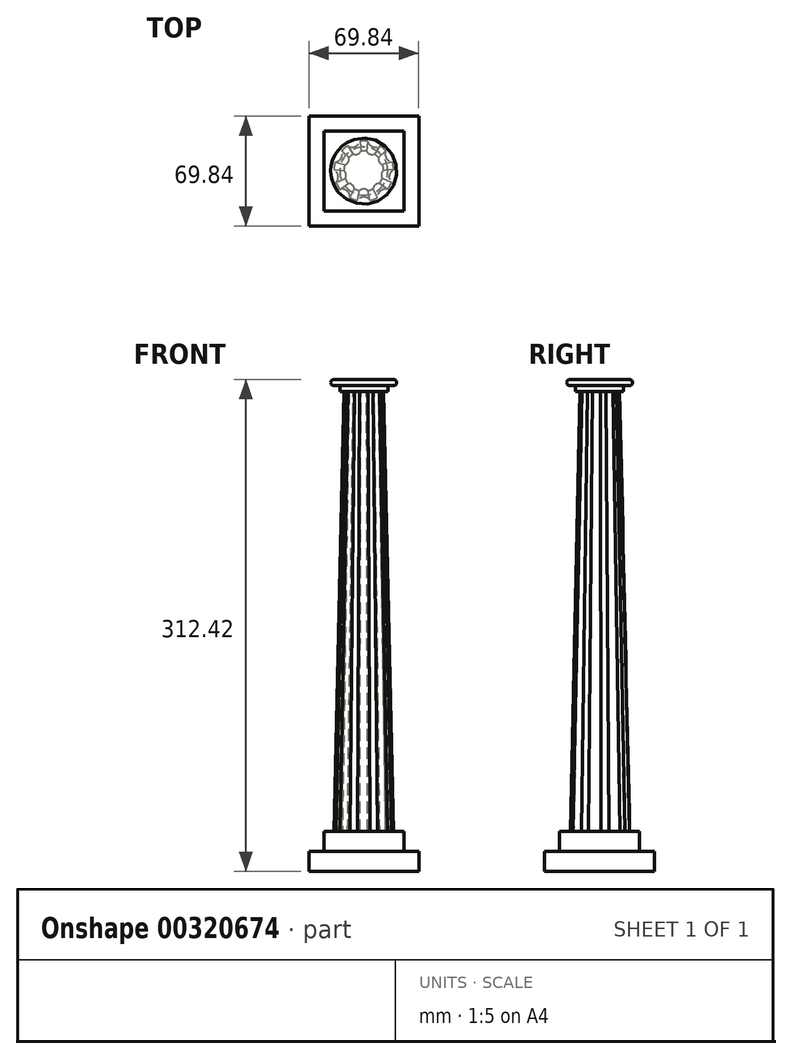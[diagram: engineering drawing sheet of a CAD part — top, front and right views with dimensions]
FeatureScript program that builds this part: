
annotation { "Feature Type Name" : "Feature", "Feature Type Description" : "" }
export const myFeature = defineFeature(function(context is Context, id is Id, definition is map)
    precondition{}
    {
        {
            var Q0;
            Q0=qCreatedBy(makeId("Top.planeOp"),FACE);
            var sketch = newSketch(context, id + "F0", { "sketchPlane" : qUnion([Q0])});
            skLineSegment(sketch, "E0.bottom", {"start": v(34.93, -34.93) * mm, "end": v(-34.92, -34.93) * mm});
            skLineSegment(sketch, "E0.top", {"start": v(34.92, 34.93) * mm, "end": v(-34.93, 34.92) * mm});
            skLineSegment(sketch, "E0.left", {"start": v(34.93, -34.93) * mm, "end": v(34.92, 34.93) * mm});
            skLineSegment(sketch, "E0.right", {"start": v(-34.92, -34.93) * mm, "end": v(-34.93, 34.92) * mm});
            skPoint(sketch, "E0.middle", {"position": v(0, 0) * mm});
            skSolve(sketch);
        }
        {
            var Q0;
            Q0=makeQuery(id+"F0.imprint","IMPRINT",FACE,{"disambiguationData":[TD([[makeQuery(id+"F0.imprint","IMPRINT",EDGE,{"derivedFrom":sQuery(id+"F0.wireOp",EDGE,"E0.bottom")}),-1.0]])]});
            extrude(context, id + "F1", {"entities" : qUnion([Q0]), "depth" : 12.7 * mm});
        }
        {
            var Q0;
            Q0=makeQuery(id+"F1.opExtrude","CAP_FACE",FACE,{"disambiguationData":[OSD([sQuery(id+"F0.wireOp",EDGE,"E0.bottom"),sQuery(id+"F0.wireOp",EDGE,"E0.top"),sQuery(id+"F0.wireOp",EDGE,"E0.left"),sQuery(id+"F0.wireOp",EDGE,"E0.right")])],"isStart":false});
            var sketch = newSketch(context, id + "F2", { "sketchPlane" : qUnion([Q0])});
            skLineSegment(sketch, "E1.bottom", {"start": v(25.4, -25.4) * mm, "end": v(-25.4, -25.4) * mm});
            skLineSegment(sketch, "E1.top", {"start": v(25.4, 25.4) * mm, "end": v(-25.4, 25.4) * mm});
            skLineSegment(sketch, "E1.left", {"start": v(25.4, -25.4) * mm, "end": v(25.4, 25.4) * mm});
            skLineSegment(sketch, "E1.right", {"start": v(-25.4, -25.4) * mm, "end": v(-25.4, 25.4) * mm});
            skPoint(sketch, "E1.middle", {"position": v(0, 0) * mm});
            skSolve(sketch);
        }
        {
            var Q0;
            Q0=makeQuery(id+"F2.imprint","IMPRINT",FACE,{"disambiguationData":[TD([[makeQuery(id+"F2.imprint","IMPRINT",EDGE,{"derivedFrom":sQuery(id+"F2.wireOp",EDGE,"E1.bottom")}),-1.0]])]});
            extrude(context, id + "F3", {"entities" : qUnion([Q0]), "operationType" : NewBodyOperationType.ADD, "depth" : 12.7 * mm});
        }
        {
            var Q0;
            Q0=qCreatedBy(makeId("Top.planeOp"),FACE);
            cPlane(context, id + "F4", {"entities" : qUnion([Q0]), "cplaneType" : CPlaneType.OFFSET, "offset" : 304.8 * mm, "width" : 152.4 * mm, "height" : 152.4 * mm});
        }
        {
            var Q0;
            Q0=makeQuery(id+"F3.opExtrude","CAP_FACE",FACE,{"disambiguationData":[OSD([sQuery(id+"F2.wireOp",EDGE,"E1.bottom"),sQuery(id+"F2.wireOp",EDGE,"E1.top"),sQuery(id+"F2.wireOp",EDGE,"E1.left"),sQuery(id+"F2.wireOp",EDGE,"E1.right")])],"isStart":false});
            var sketch = newSketch(context, id + "F5", { "sketchPlane" : qUnion([Q0])});
            skCircle(sketch, "E2", {"center": v(0, 0) * mm, "radius": 19.05 * mm});
            skPoint(sketch, "E3", {"position": v(0, -21.59) * mm});
            skArc(sketch, "E4", {"start": v(4.1, -18.6) * mm, "mid": v(0, -16.51) * mm, "end": v(-4.1, -18.6) * mm});
            skArc(sketch, "E5.1.0", {"start": v(15.1, -11.6) * mm, "mid": v(10.61, -12.65) * mm, "end": v(8.8, -16.9) * mm});
            skArc(sketch, "E5.2.0", {"start": v(19.03, 0.82) * mm, "mid": v(16.26, -2.87) * mm, "end": v(17.6, -7.28) * mm});
            skArc(sketch, "E5.3.0", {"start": v(14.06, 12.86) * mm, "mid": v(14.3, 8.25) * mm, "end": v(18.16, 5.74) * mm});
            skArc(sketch, "E5.4.0", {"start": v(2.5, 18.89) * mm, "mid": v(5.65, 15.51) * mm, "end": v(10.22, 16.07) * mm});
            skArc(sketch, "E5.5.0", {"start": v(-10.22, 16.07) * mm, "mid": v(-5.65, 15.51) * mm, "end": v(-2.5, 18.89) * mm});
            skArc(sketch, "E5.6.0", {"start": v(-18.16, 5.74) * mm, "mid": v(-14.3, 8.26) * mm, "end": v(-14.06, 12.86) * mm});
            skArc(sketch, "E5.7.0", {"start": v(-17.6, -7.28) * mm, "mid": v(-16.26, -2.87) * mm, "end": v(-19.03, 0.82) * mm});
            skArc(sketch, "E5.8.0", {"start": v(-8.8, -16.9) * mm, "mid": v(-10.61, -12.65) * mm, "end": v(-15.1, -11.6) * mm});
            skSolve(sketch);
        }
        {
            var Q0;
            Q0=qCreatedBy(id+"F4.planeOp",FACE);
            var sketch = newSketch(context, id + "F6", { "sketchPlane" : qUnion([Q0])});
            skCircle(sketch, "E6", {"center": v(0, 0) * mm, "radius": 12.7 * mm});
            skPoint(sketch, "E7", {"position": v(0, -15.24) * mm});
            skArc(sketch, "E8", {"start": v(2.58, -12.44) * mm, "mid": v(0, -11.43) * mm, "end": v(-2.58, -12.44) * mm});
            skArc(sketch, "E9.1.0", {"start": v(9.97, -7.87) * mm, "mid": v(7.35, -8.76) * mm, "end": v(6.02, -11.18) * mm});
            skArc(sketch, "E9.2.0", {"start": v(12.7, 0.38) * mm, "mid": v(11.26, -1.98) * mm, "end": v(11.8, -4.7) * mm});
            skArc(sketch, "E9.3.0", {"start": v(9.48, 8.45) * mm, "mid": v(9.9, 5.71) * mm, "end": v(12.06, 3.98) * mm});
            skArc(sketch, "E9.4.0", {"start": v(1.83, 12.57) * mm, "mid": v(3.9, 10.74) * mm, "end": v(6.68, 10.8) * mm});
            skArc(sketch, "E9.5.0", {"start": v(-6.68, 10.8) * mm, "mid": v(-3.9, 10.74) * mm, "end": v(-1.83, 12.57) * mm});
            skArc(sketch, "E9.6.0", {"start": v(-12.06, 3.98) * mm, "mid": v(-9.9, 5.72) * mm, "end": v(-9.48, 8.45) * mm});
            skArc(sketch, "E9.7.0", {"start": v(-11.8, -4.7) * mm, "mid": v(-11.26, -1.98) * mm, "end": v(-12.7, 0.38) * mm});
            skArc(sketch, "E9.8.0", {"start": v(-6.02, -11.18) * mm, "mid": v(-7.35, -8.76) * mm, "end": v(-9.97, -7.87) * mm});
            skSolve(sketch);
        }
        {
            var Q1;
            {var subQ0=sQuery(id+"F5.wireOp",EDGE,"E4");Q1=makeQuery(id+"F5.imprint","IMPRINT",FACE,{"disambiguationData":[TD([[makeQuery(id+"F5.imprint","IMPRINT",EDGE,{"derivedFrom":subQ0}),-1.0]])]});}
            var Q2;
            {var subQ0=sQuery(id+"F6.wireOp",EDGE,"E8");Q2=makeQuery(id+"F6.imprint","IMPRINT",FACE,{"disambiguationData":[TD([[makeQuery(id+"F6.imprint","IMPRINT",EDGE,{"derivedFrom":subQ0}),-1.0]])]});}
            loft(context, id + "F7", {"operationType" : NewBodyOperationType.ADD, "sheetProfilesArray" : [{ "sheetProfileEntities" : qUnion([Q1]) }, { "sheetProfileEntities" : qUnion([Q2]) }]});
        }
        {
            var Q0;
            Q0=qCreatedBy(makeId("Right.planeOp"),FACE);
            var sketch = newSketch(context, id + "F8", { "sketchPlane" : qUnion([Q0])});
            skPoint(sketch, "E10", {"position": v(0, 304.8) * mm});
            skLineSegment(sketch, "E11.bottom", {"start": v(0, 304.8) * mm, "end": v(15.24, 304.8) * mm});
            skLineSegment(sketch, "E11.top", {"start": v(0, 312.42) * mm, "end": v(15.24, 312.42) * mm});
            skLineSegment(sketch, "E11.left", {"start": v(0, 304.8) * mm, "end": v(0, 312.42) * mm});
            skLineSegment(sketch, "E11.right", {"start": v(15.24, 304.8) * mm, "end": v(15.24, 312.42) * mm});
            skLineSegment(sketch, "E12.bottom", {"start": v(15.24, 312.42) * mm, "end": v(19.05, 312.42) * mm});
            skLineSegment(sketch, "E12.top", {"start": v(15.24, 308.61) * mm, "end": v(19.05, 308.61) * mm});
            skLineSegment(sketch, "E12.left", {"start": v(15.24, 312.42) * mm, "end": v(15.24, 308.61) * mm});
            skLineSegment(sketch, "E12.right", {"start": v(19.05, 312.42) * mm, "end": v(19.05, 308.61) * mm});
            skArc(sketch, "E13", {"start": v(19.05, 312.42) * mm, "mid": v(20.95, 310.52) * mm, "end": v(19.05, 308.61) * mm});
            skSolve(sketch);
        }
        {
            var Q0;
            Q0=makeQuery(id+"F8.imprint","IMPRINT",FACE,{"disambiguationData":[TD([[makeQuery(id+"F8.imprint","IMPRINT",EDGE,{"derivedFrom":sQuery(id+"F8.wireOp",EDGE,"E12.bottom")}),-1.0]])]});
            var Q1;
            Q1=makeQuery(id+"F8.imprint","IMPRINT",FACE,{"disambiguationData":[TD([[makeQuery(id+"F8.imprint","IMPRINT",EDGE,{"derivedFrom":sQuery(id+"F8.wireOp",EDGE,"E12.right")}),1.0]])]});
            var Q2;
            Q2=makeQuery(id+"F8.imprint","IMPRINT",FACE,{"disambiguationData":[TD([[makeQuery(id+"F8.imprint","IMPRINT",EDGE,{"derivedFrom":sQuery(id+"F8.wireOp",EDGE,"E11.bottom")}),1.0]])]});
            var Q3;
            Q3=sQuery(id+"F8.wireOp",EDGE,"E11.left");
            revolve(context, id + "F9", {"operationType" : NewBodyOperationType.ADD, "entities" : qUnion([Q0, Q1, Q2]), "axis" : qUnion([Q3]), "revolveType" : RevolveType.FULL});
        }
    });
